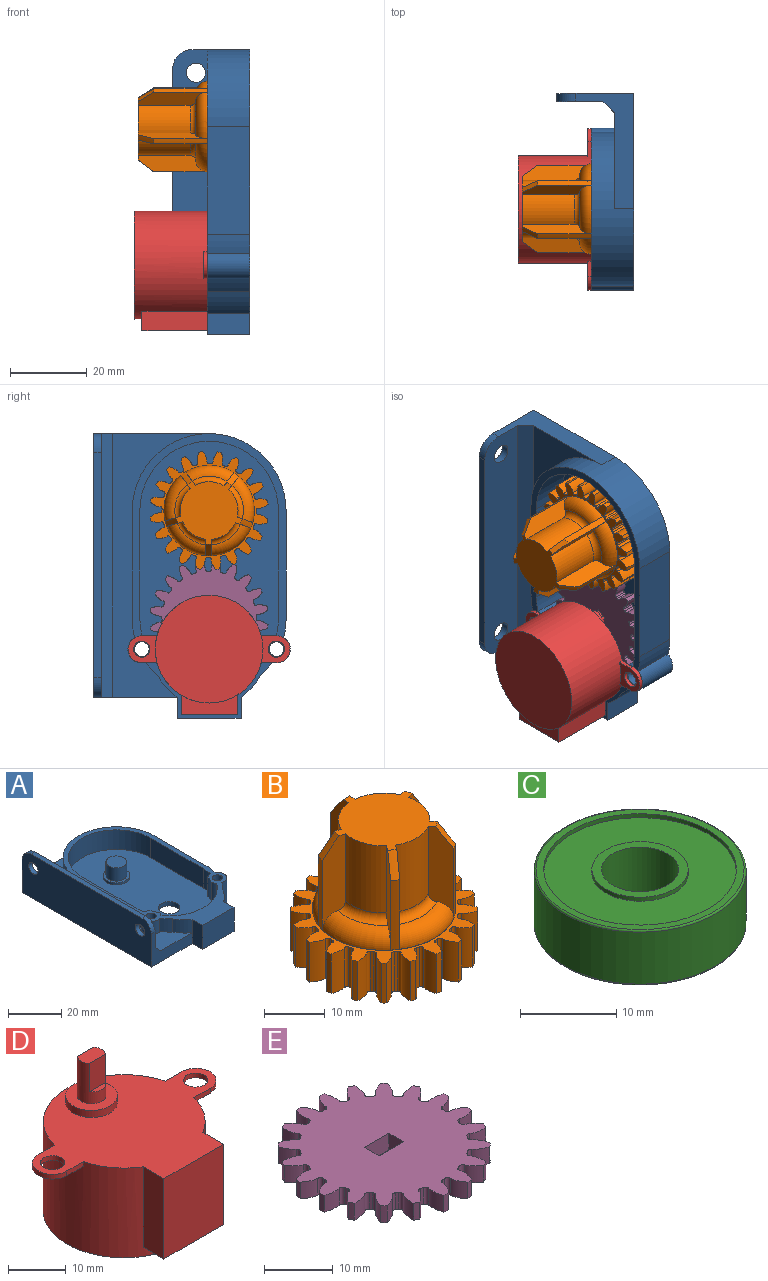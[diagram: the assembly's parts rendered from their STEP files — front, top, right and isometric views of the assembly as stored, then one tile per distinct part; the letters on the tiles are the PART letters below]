
ASSEMBLY  parts=5 mates=4
PART A: 47 faces, bbox 51.1x74x20 mm
  f0: cylinder r=3.6mm len=9mm, axis (0,0,-1), area 19.2mm2, adj f10,f23,f31,f46
  f1: cylinder r=3.6mm len=9mm, axis (0,0,-1), area 19.2mm2, adj f10,f13,f31,f45
  f2: plane 68.49x12mm, normal (1,0,0), area 771.9mm2, adj f36,f37,f39,f40,f41,f42,f43,f44
  f3: plane 68.49x20mm, normal (-1,0,0), area 1319.9mm2, adj f11,f36,f37,f39,f41,f42,f43,f44
  f4: cylinder r=20mm len=11mm, axis (0,0,-1), area 54.8mm2, adj f5,f11,f15,f31
  f5: plane 28x11mm, normal (1,0,0), area 308mm2, adj f4,f6,f11,f31
  f6: cylinder r=20mm len=40mm, axis (0,0,-1), area 534.1mm2, adj f5,f7,f11,f31,f36,f38
  f7: plane 28x6mm, normal (-1,0,0), area 168mm2, adj f6,f8,f31,f38
  f8: cylinder r=20mm len=6mm, axis (0,0,-1), area 29.9mm2, adj f7,f16,f31,f38
  f9: cylinder r=4mm len=8mm, axis (0,0,-1), area 50.3mm2, adj f10,f11
  f10: plane 64x36mm, normal (0,0,1), area 1878.3mm2, adj f0,f1,f9,f12,f13,f14,f23,f24
  f11: plane 74x51.1mm, normal (0,0,-1), area 3293.5mm2, adj f3,f4,f5,f6,f9,f15,f19,f20
  f12: cylinder r=3.6mm len=9mm, axis (0,0,-1), area 19.2mm2, adj f10,f13,f31,f46
  f13: cylinder r=18mm len=29.5mm, axis (0,0,-1), area 311.1mm2, adj f1,f10,f12,f31
  f14: cylinder r=3.6mm len=9mm, axis (0,0,-1), area 19.2mm2, adj f10,f24,f31,f45
  f15: cylinder r=3.6mm len=11mm, axis (0,0,-1), area 114.8mm2, adj f4,f11,f28,f31
  f16: cylinder r=3.6mm len=6.67mm, axis (0,0,-1), area 62.6mm2, adj f8,f17,f31,f38
  f17: cylinder r=20mm len=6mm, axis (0,0,-1), area 28.2mm2, adj f16,f18,f31,f38
  f18: cylinder r=15mm len=6mm, axis (0,0,-1), area 45.3mm2, adj f17,f19,f31,f38
  f19: plane 11x5.51mm, normal (-1,0,0), area 60.6mm2, adj f11,f18,f20,f31,f37
  f20: plane 16.6x11mm, normal (0,-1,0), area 182.6mm2, adj f11,f19,f21,f31
  f21: plane 11x5.51mm, normal (1,0,0), area 60.6mm2, adj f11,f20,f22,f31
  f22: cylinder r=15mm len=11mm, axis (0,0,-1), area 83.1mm2, adj f11,f21,f28,f31
  f23: cylinder r=18mm len=9mm, axis (0,0,-1), area 40mm2, adj f0,f10,f29,f31
  f24: cylinder r=18mm len=9mm, axis (0,0,-1), area 40mm2, adj f10,f14,f25,f31
  f25: plane 28x9mm, normal (1,0,0), area 252mm2, adj f10,f24,f26,f31
  f26: cylinder r=18mm len=36mm, axis (0,0,-1), area 508.9mm2, adj f10,f25,f29,f31
  f27: cylinder r=1.9mm len=11mm, axis (0,0,-1), area 131.3mm2, adj f11,f31
  f28: cylinder r=20mm len=11mm, axis (0,0,-1), area 51.7mm2, adj f11,f15,f22,f31
  f29: plane 28x9mm, normal (-1,0,0), area 252mm2, adj f10,f23,f26,f31
  f30: cylinder r=1.9mm len=11mm, axis (0,0,-1), area 131.3mm2, adj f11,f31
  f31: plane 74x42.2mm, normal (0,0,1), area 502.1mm2, adj f0,f1,f4,f5,f6,f7,f8,f12
  f32: cylinder r=5mm len=10mm, axis (0,0,-1), area 31.4mm2, adj f10,f33
  f33: plane 10x10mm, normal (0,0,1), area 30.8mm2, adj f32,f35
  f34: plane 7.8x7.8mm, normal (0,0,1), area 47.8mm2, adj f35
  f35: cylinder r=3.9mm len=7.8mm, axis (0,0,-1), area 147mm2, adj f33,f34
  f36: plane 30x15mm, normal (0,1,0), area 174.5mm2, adj f2,f3,f6,f11,f38,f40,f43
  f37: plane 21.7x15mm, normal (0,-1,0), area 133mm2, adj f2,f3,f11,f19,f38,f40,f44
  f38: plane 68.49x25mm, normal (0,0,1), area 492.1mm2, adj f6,f7,f8,f16,f17,f18,f36,f37
  f39: plane 58.49x2mm, normal (0,0,1), area 117mm2, adj f2,f3,f43,f44
  f40: plane 68.49x3mm, normal (0.71,0,0.71), area 290.6mm2, adj f2,f36,f37,f38
  f41: cylinder r=2.5mm len=5mm, axis (1,0,0), area 31.4mm2, adj f2,f3
  f42: cylinder r=2.5mm len=5mm, axis (1,0,0), area 31.4mm2, adj f2,f3
  f43: cylinder r=5mm len=5mm, axis (1,0,0), area 15.7mm2, adj f2,f3,f36,f39
  f44: cylinder r=5mm len=5mm, axis (-1,0,0), area 15.7mm2, adj f2,f3,f37,f39
  f45: cylinder r=16.25mm len=9mm, axis (0,0,1), area 33.1mm2, adj f1,f10,f14,f31
  f46: cylinder r=16.25mm len=9mm, axis (0,0,1), area 33.1mm2, adj f0,f10,f12,f31
PART B: 156 faces, bbox 30.6x30.6x26 mm
  f0: cylinder r=15.4mm len=8mm, axis (0,0,-1), area 7.8mm2, adj f19,f21,f72,f119
  f1: cylinder r=15.4mm len=8mm, axis (0,0,-1), area 7.8mm2, adj f19,f21,f114,f117
  f2: cylinder r=15.4mm len=8mm, axis (0,0,-1), area 7.8mm2, adj f19,f21,f109,f112
  f3: cylinder r=15.4mm len=8mm, axis (0,0,-1), area 7.8mm2, adj f19,f21,f104,f107
  f4: cylinder r=15.4mm len=8mm, axis (0,0,-1), area 7.8mm2, adj f19,f21,f99,f102
  f5: cylinder r=15.4mm len=8mm, axis (0,0,-1), area 7.8mm2, adj f19,f21,f94,f97
  f6: cylinder r=15.4mm len=8mm, axis (0,0,-1), area 7.8mm2, adj f19,f21,f89,f92
  f7: cylinder r=15.4mm len=8mm, axis (0,0,-1), area 7.8mm2, adj f19,f21,f84,f87
  f8: cylinder r=15.4mm len=8mm, axis (0,0,-1), area 7.8mm2, adj f19,f21,f67,f79
  f9: cylinder r=15.4mm len=8mm, axis (0,0,-1), area 7.8mm2, adj f19,f21,f74,f77
  f10: cylinder r=15.4mm len=8mm, axis (0,0,-1), area 7.8mm2, adj f19,f21,f62,f69
  f11: cylinder r=15.4mm len=8mm, axis (0,0,-1), area 7.8mm2, adj f19,f21,f42,f64
  f12: cylinder r=15.4mm len=8mm, axis (0,0,-1), area 7.8mm2, adj f19,f21,f22,f59
  f13: cylinder r=15.4mm len=8mm, axis (0,0,-1), area 7.8mm2, adj f19,f21,f54,f57
  f14: cylinder r=15.4mm len=8mm, axis (0,0,-1), area 7.8mm2, adj f19,f21,f49,f52
  f15: cylinder r=15.4mm len=8mm, axis (0,0,-1), area 7.8mm2, adj f19,f21,f44,f47
  f16: cylinder r=15.4mm len=8mm, axis (0,0,-1), area 7.8mm2, adj f19,f21,f32,f39
  f17: cylinder r=15.4mm len=8mm, axis (0,0,-1), area 7.8mm2, adj f19,f21,f34,f82
  f18: cylinder r=15.4mm len=8mm, axis (0,0,-1), area 7.8mm2, adj f19,f21,f29,f37
  f19: plane 30.58x30.58mm, normal (0,0,1), area 169.5mm2, adj f0,f1,f2,f3,f4,f5,f6,f7
  f20: cylinder r=15.4mm len=8mm, axis (0,0,-1), area 7.8mm2, adj f19,f21,f24,f27
  f21: plane 30.58x30.58mm, normal (0,0,-1), area 216.2mm2, adj f0,f1,f2,f3,f4,f5,f6,f7
  f22: extruded ~8x2.51mm, area 22.5mm2, adj f12,f19,f21,f25
  f23: cylinder r=12.25mm len=8mm, axis (0,0,-1), area 4mm2, adj f19,f21,f25,f26
  f24: extruded ~8x2.51mm, area 22.5mm2, adj f19,f20,f21,f26
  f25: cylinder r=0.55mm len=8mm, axis (0,0,-1), area 6.8mm2, adj f19,f21,f22,f23
  f26: cylinder r=0.55mm len=8mm, axis (0,0,-1), area 6.8mm2, adj f19,f21,f23,f24
  f27: extruded ~8x2.73mm, area 22.5mm2, adj f19,f20,f21,f30
  f28: cylinder r=12.25mm len=8mm, axis (0,0,-1), area 4mm2, adj f19,f21,f30,f31
  f29: extruded ~8x2.05mm, area 22.5mm2, adj f18,f19,f21,f31
  f30: cylinder r=0.55mm len=8mm, axis (0,0,-1), area 6.8mm2, adj f19,f21,f27,f28
  f31: cylinder r=0.55mm len=8mm, axis (0,0,-1), area 6.8mm2, adj f19,f21,f28,f29
  f32: extruded ~8x2.38mm, area 22.5mm2, adj f16,f19,f21,f35
  f33: cylinder r=12.25mm len=8mm, axis (0,0,-1), area 4mm2, adj f19,f21,f35,f36
  f34: extruded ~8x2.69mm, area 22.5mm2, adj f17,f19,f21,f36
  f35: cylinder r=0.55mm len=8mm, axis (0,0,-1), area 6.8mm2, adj f19,f21,f32,f33
  f36: cylinder r=0.55mm len=8mm, axis (0,0,-1), area 6.8mm2, adj f19,f21,f33,f34
  f37: extruded ~8x2.69mm, area 22.5mm2, adj f18,f19,f21,f40
  f38: cylinder r=12.25mm len=8mm, axis (0,0,-1), area 4mm2, adj f19,f21,f40,f41
  f39: extruded ~8x2.38mm, area 22.5mm2, adj f16,f19,f21,f41
  f40: cylinder r=0.55mm len=8mm, axis (0,0,-1), area 6.8mm2, adj f19,f21,f37,f38
  f41: cylinder r=0.55mm len=8mm, axis (0,0,-1), area 6.8mm2, adj f19,f21,f38,f39
  f42: extruded ~8x2.73mm, area 22.5mm2, adj f11,f19,f21,f45
  f43: cylinder r=12.25mm len=8mm, axis (0,0,-1), area 4mm2, adj f19,f21,f45,f46
  f44: extruded ~8x2.05mm, area 22.5mm2, adj f15,f19,f21,f46
  f45: cylinder r=0.55mm len=8mm, axis (0,0,-1), area 6.8mm2, adj f19,f21,f42,f43
  f46: cylinder r=0.55mm len=8mm, axis (0,0,-1), area 6.8mm2, adj f19,f21,f43,f44
  f47: extruded ~8x2.69mm, area 22.5mm2, adj f15,f19,f21,f50
  f48: cylinder r=12.25mm len=8mm, axis (0,0,-1), area 4mm2, adj f19,f21,f50,f51
  f49: extruded ~8x2.38mm, area 22.5mm2, adj f14,f19,f21,f51
  f50: cylinder r=0.55mm len=8mm, axis (0,0,-1), area 6.8mm2, adj f19,f21,f47,f48
  f51: cylinder r=0.55mm len=8mm, axis (0,0,-1), area 6.8mm2, adj f19,f21,f48,f49
  f52: extruded ~8x2.38mm, area 22.5mm2, adj f14,f19,f21,f55
  f53: cylinder r=12.25mm len=8mm, axis (0,0,-1), area 4mm2, adj f19,f21,f55,f56
  f54: extruded ~8x2.69mm, area 22.5mm2, adj f13,f19,f21,f56
  f55: cylinder r=0.55mm len=8mm, axis (0,0,-1), area 6.8mm2, adj f19,f21,f52,f53
  f56: cylinder r=0.55mm len=8mm, axis (0,0,-1), area 6.8mm2, adj f19,f21,f53,f54
  f57: extruded ~8x2.05mm, area 22.5mm2, adj f13,f19,f21,f60
  f58: cylinder r=12.25mm len=8mm, axis (0,0,-1), area 4mm2, adj f19,f21,f60,f61
  f59: extruded ~8x2.73mm, area 22.5mm2, adj f12,f19,f21,f61
  f60: cylinder r=0.55mm len=8mm, axis (0,0,-1), area 6.8mm2, adj f19,f21,f57,f58
  f61: cylinder r=0.55mm len=8mm, axis (0,0,-1), area 6.8mm2, adj f19,f21,f58,f59
  f62: extruded ~8x2.51mm, area 22.5mm2, adj f10,f19,f21,f65
  f63: cylinder r=12.25mm len=8mm, axis (0,0,-1), area 4mm2, adj f19,f21,f65,f66
  f64: extruded ~8x2.51mm, area 22.5mm2, adj f11,f19,f21,f66
  f65: cylinder r=0.55mm len=8mm, axis (0,0,-1), area 6.8mm2, adj f19,f21,f62,f63
  f66: cylinder r=0.55mm len=8mm, axis (0,0,-1), area 6.8mm2, adj f19,f21,f63,f64
  f67: extruded ~8x2.05mm, area 22.5mm2, adj f8,f19,f21,f70
  f68: cylinder r=12.25mm len=8mm, axis (0,0,-1), area 4mm2, adj f19,f21,f70,f71
  f69: extruded ~8x2.73mm, area 22.5mm2, adj f10,f19,f21,f71
  f70: cylinder r=0.55mm len=8mm, axis (0,0,-1), area 6.8mm2, adj f19,f21,f67,f68
  f71: cylinder r=0.55mm len=8mm, axis (0,0,-1), area 6.8mm2, adj f19,f21,f68,f69
  f72: extruded ~8x2.69mm, area 22.5mm2, adj f0,f19,f21,f75
  f73: cylinder r=12.25mm len=8mm, axis (0,0,-1), area 4mm2, adj f19,f21,f75,f76
  f74: extruded ~8x2.38mm, area 22.5mm2, adj f9,f19,f21,f76
  f75: cylinder r=0.55mm len=8mm, axis (0,0,-1), area 6.8mm2, adj f19,f21,f72,f73
  f76: cylinder r=0.55mm len=8mm, axis (0,0,-1), area 6.8mm2, adj f19,f21,f73,f74
  f77: extruded ~8x2.38mm, area 22.5mm2, adj f9,f19,f21,f80
  f78: cylinder r=12.25mm len=8mm, axis (0,0,-1), area 4mm2, adj f19,f21,f80,f81
  f79: extruded ~8x2.69mm, area 22.5mm2, adj f8,f19,f21,f81
  f80: cylinder r=0.55mm len=8mm, axis (0,0,-1), area 6.8mm2, adj f19,f21,f77,f78
  f81: cylinder r=0.55mm len=8mm, axis (0,0,-1), area 6.8mm2, adj f19,f21,f78,f79
  f82: extruded ~8x2.05mm, area 22.5mm2, adj f17,f19,f21,f85
  f83: cylinder r=12.25mm len=8mm, axis (0,0,-1), area 4mm2, adj f19,f21,f85,f86
  f84: extruded ~8x2.73mm, area 22.5mm2, adj f7,f19,f21,f86
  f85: cylinder r=0.55mm len=8mm, axis (0,0,-1), area 6.8mm2, adj f19,f21,f82,f83
  f86: cylinder r=0.55mm len=8mm, axis (0,0,-1), area 6.8mm2, adj f19,f21,f83,f84
  f87: extruded ~8x2.51mm, area 22.5mm2, adj f7,f19,f21,f90
  f88: cylinder r=12.25mm len=8mm, axis (0,0,-1), area 4mm2, adj f19,f21,f90,f91
  f89: extruded ~8x2.51mm, area 22.5mm2, adj f6,f19,f21,f91
  f90: cylinder r=0.55mm len=8mm, axis (0,0,-1), area 6.8mm2, adj f19,f21,f87,f88
  f91: cylinder r=0.55mm len=8mm, axis (0,0,-1), area 6.8mm2, adj f19,f21,f88,f89
  f92: extruded ~8x2.73mm, area 22.5mm2, adj f6,f19,f21,f95
  f93: cylinder r=12.25mm len=8mm, axis (0,0,-1), area 4mm2, adj f19,f21,f95,f96
  f94: extruded ~8x2.05mm, area 22.5mm2, adj f5,f19,f21,f96
  f95: cylinder r=0.55mm len=8mm, axis (0,0,-1), area 6.8mm2, adj f19,f21,f92,f93
  f96: cylinder r=0.55mm len=8mm, axis (0,0,-1), area 6.8mm2, adj f19,f21,f93,f94
  f97: extruded ~8x2.69mm, area 22.5mm2, adj f5,f19,f21,f100
  f98: cylinder r=12.25mm len=8mm, axis (0,0,-1), area 4mm2, adj f19,f21,f100,f101
  f99: extruded ~8x2.38mm, area 22.5mm2, adj f4,f19,f21,f101
  f100: cylinder r=0.55mm len=8mm, axis (0,0,-1), area 6.8mm2, adj f19,f21,f97,f98
  f101: cylinder r=0.55mm len=8mm, axis (0,0,-1), area 6.8mm2, adj f19,f21,f98,f99
  f102: extruded ~8x2.38mm, area 22.5mm2, adj f4,f19,f21,f105
  f103: cylinder r=12.25mm len=8mm, axis (0,0,-1), area 4mm2, adj f19,f21,f105,f106
  f104: extruded ~8x2.69mm, area 22.5mm2, adj f3,f19,f21,f106
  f105: cylinder r=0.55mm len=8mm, axis (0,0,-1), area 6.8mm2, adj f19,f21,f102,f103
  f106: cylinder r=0.55mm len=8mm, axis (0,0,-1), area 6.8mm2, adj f19,f21,f103,f104
  f107: extruded ~8x2.05mm, area 22.5mm2, adj f3,f19,f21,f110
  f108: cylinder r=12.25mm len=8mm, axis (0,0,-1), area 4mm2, adj f19,f21,f110,f111
  f109: extruded ~8x2.73mm, area 22.5mm2, adj f2,f19,f21,f111
  f110: cylinder r=0.55mm len=8mm, axis (0,0,-1), area 6.8mm2, adj f19,f21,f107,f108
  f111: cylinder r=0.55mm len=8mm, axis (0,0,-1), area 6.8mm2, adj f19,f21,f108,f109
  f112: extruded ~8x2.51mm, area 22.5mm2, adj f2,f19,f21,f115
  f113: cylinder r=12.25mm len=8mm, axis (0,0,-1), area 4mm2, adj f19,f21,f115,f116
  f114: extruded ~8x2.51mm, area 22.5mm2, adj f1,f19,f21,f116
  f115: cylinder r=0.55mm len=8mm, axis (0,0,-1), area 6.8mm2, adj f19,f21,f112,f113
  f116: cylinder r=0.55mm len=8mm, axis (0,0,-1), area 6.8mm2, adj f19,f21,f113,f114
  f117: extruded ~8x2.73mm, area 22.5mm2, adj f1,f19,f21,f120
  f118: cylinder r=12.25mm len=8mm, axis (0,0,-1), area 4mm2, adj f19,f21,f120,f121
  f119: extruded ~8x2.05mm, area 22.5mm2, adj f0,f19,f21,f121
  f120: cylinder r=0.55mm len=8mm, axis (0,0,-1), area 6.8mm2, adj f19,f21,f117,f118
  f121: cylinder r=0.55mm len=8mm, axis (0,0,-1), area 6.8mm2, adj f19,f21,f118,f119
  f122: cylinder r=11.75mm len=23.5mm, axis (0,0,-1), area 105.5mm2, adj f19,f124,f125,f127,f128,f130,f131,f133
  f123: cylinder r=7.5mm len=13.5mm, axis (0,0,-1), area 107mm2, adj f124,f137,f138,f150
  f124: plane 18.04x3.49mm, normal (-0.81,-0.59,0), area 59.4mm2, adj f122,f123,f138,f140,f150,f151
  f125: plane 18.04x3.49mm, normal (0.81,0.59,0), area 59.4mm2, adj f122,f126,f138,f140,f149,f155
  f126: cylinder r=7.5mm len=13.5mm, axis (0,0,-1), area 107mm2, adj f125,f127,f138,f149
  f127: plane 18.04x4.1mm, normal (0.31,-0.95,0), area 59.4mm2, adj f122,f126,f138,f139,f149,f155
  f128: plane 18.04x4.1mm, normal (-0.31,0.95,0), area 59.4mm2, adj f122,f129,f138,f139,f148,f154
  f129: cylinder r=7.5mm len=13.5mm, axis (0,0,-1), area 107mm2, adj f128,f130,f138,f148
  f130: plane 18.04x4.31mm, normal (1,0,0), area 59.4mm2, adj f122,f129,f138,f142,f148,f154
  f131: plane 18.04x4.31mm, normal (-1,0,0), area 59.4mm2, adj f122,f132,f138,f142,f147,f153
  f132: cylinder r=7.5mm len=13.5mm, axis (0,0,-1), area 107mm2, adj f131,f133,f138,f147
  f133: plane 18.04x4.1mm, normal (0.31,0.95,0), area 59.4mm2, adj f122,f132,f138,f143,f147,f153
  f134: plane 18.04x4.1mm, normal (-0.31,-0.95,0), area 59.4mm2, adj f122,f135,f138,f143,f146,f152
  f135: cylinder r=7.5mm len=13.5mm, axis (0,0,-1), area 107mm2, adj f134,f136,f138,f146
  f136: plane 18.04x3.49mm, normal (-0.81,0.59,0), area 59.4mm2, adj f122,f135,f138,f141,f146,f152
  f137: plane 18.04x3.49mm, normal (0.81,-0.59,0), area 59.4mm2, adj f122,f123,f138,f141,f150,f151
  f138: plane 17.05x16.25mm, normal (0,0,1), area 186.1mm2, adj f123,f124,f125,f126,f127,f128,f129,f130
  f139: cone r=8.75mm half-angle=36.9deg, axis (0,0,-1), area 7.6mm2, adj f122,f127,f128,f138
  f140: cone r=8.75mm half-angle=36.9deg, axis (0,0,-1), area 7.6mm2, adj f122,f124,f125,f138
  f141: cone r=8.75mm half-angle=36.9deg, axis (0,0,-1), area 7.6mm2, adj f122,f136,f137,f138
  f142: cone r=8.75mm half-angle=36.9deg, axis (0,0,-1), area 7.6mm2, adj f122,f130,f131,f138
  f143: cone r=8.75mm half-angle=36.9deg, axis (0,0,-1), area 7.6mm2, adj f122,f133,f134,f138
  f144: cylinder r=11.1mm len=22.2mm, axis (0,0,-1), area 557.9mm2, adj f21,f145
  f145: plane 22.2x22.2mm, normal (0,0,-1), area 387.1mm2, adj f144
  f146: torus R=9mm, axis (0,0,1), area 19.5mm2, adj f134,f135,f136,f152
  f147: torus R=9mm, axis (0,0,1), area 19.5mm2, adj f131,f132,f133,f153
  f148: torus R=9mm, axis (0,0,1), area 19.5mm2, adj f128,f129,f130,f154
  f149: torus R=9mm, axis (0,0,1), area 19.5mm2, adj f125,f126,f127,f155
  f150: torus R=9mm, axis (0,0,1), area 19.5mm2, adj f123,f124,f137,f151
  f151: torus R=8.75mm, axis (0,0,-1), area 54.5mm2, adj f122,f124,f137,f150
  f152: torus R=8.75mm, axis (0,0,-1), area 54.5mm2, adj f122,f134,f136,f146
  f153: torus R=8.75mm, axis (0,0,-1), area 54.4mm2, adj f122,f131,f133,f147
  f154: torus R=8.75mm, axis (0,0,-1), area 54.4mm2, adj f122,f128,f130,f148
  f155: torus R=8.75mm, axis (0,0,-1), area 54.4mm2, adj f122,f125,f127,f149
PART C: 14 faces, bbox 23.8x23.8x7 mm
  f0: plane 10x10mm, normal (0,0,-1), area 28.3mm2, adj f2,f9
  f1: plane 10x10mm, normal (0,0,1), area 28.3mm2, adj f2,f6
  f2: cylinder r=4mm len=8mm, axis (0,0,-1), area 175.9mm2, adj f0,f1
  f3: cylinder r=11mm len=22mm, axis (0,0,-1), area 456.2mm2, adj f12,f13
  f4: plane 21.6x21.6mm, normal (0,0,1), area 52.3mm2, adj f7,f13
  f5: plane 21.6x21.6mm, normal (0,0,-1), area 52.3mm2, adj f10,f12
  f6: cylinder r=5mm len=10mm, axis (0,0,1), area 15.7mm2, adj f1,f8
  f7: cylinder r=10mm len=20mm, axis (0,0,1), area 31.4mm2, adj f4,f8
  f8: plane 20x20mm, normal (0,0,1), area 235.6mm2, adj f6,f7
  f9: cylinder r=5mm len=10mm, axis (0,0,-1), area 15.7mm2, adj f0,f11
  f10: cylinder r=10mm len=20mm, axis (0,0,-1), area 31.4mm2, adj f5,f11
  f11: plane 20x20mm, normal (0,0,-1), area 235.6mm2, adj f9,f10
  f12: torus R=10.8mm, axis (0,0,1), area 21.6mm2, adj f3,f5
  f13: torus R=10.8mm, axis (0,0,1), area 21.6mm2, adj f3,f4
PART D: 25 faces, bbox 42x31x29 mm
  f0: plane 28x28mm, normal (0,0,-1), area 615.8mm2, adj f11
  f1: plane 17x5.05mm, normal (-1,0,0), area 85.9mm2, adj f2,f11,f13,f16
  f2: plane 17x14.6mm, normal (0,-1,0), area 248.2mm2, adj f1,f3,f13,f16
  f3: plane 17x5.05mm, normal (1,0,0), area 85.9mm2, adj f2,f11,f13,f16
  f4: plane 3.94x1mm, normal (0,-1,0), area 3.9mm2, adj f5,f11,f13,f14
  f5: cylinder r=3.5mm len=7mm, axis (0,0,-1), area 11mm2, adj f4,f6,f13,f14
  f6: plane 3.94x1mm, normal (0,1,0), area 3.9mm2, adj f5,f11,f13,f14
  f7: plane 3.94x1mm, normal (0,1,0), area 3.9mm2, adj f8,f11,f13,f15
  f8: cylinder r=3.5mm len=7mm, axis (0,0,-1), area 11mm2, adj f7,f9,f13,f15
  f9: plane 3.94x1mm, normal (0,-1,0), area 3.9mm2, adj f8,f11,f13,f15
  f10: cylinder r=2.1mm len=4.2mm, axis (0,0,-1), area 13.2mm2, adj f13,f15
  f11: cylinder r=14mm len=28mm, axis (0,0,-1), area 1396.1mm2, adj f0,f1,f3,f4,f6,f7,f9,f13
  f12: cylinder r=2.1mm len=4.2mm, axis (0,0,-1), area 13.2mm2, adj f13,f14
  f13: plane 42x31mm, normal (0,0,1), area 667.5mm2, adj f1,f2,f3,f4,f5,f6,f7,f8
  f14: plane 7.44x7mm, normal (0,0,-1), area 30.9mm2, adj f4,f5,f6,f11,f12
  f15: plane 7.44x7mm, normal (0,0,-1), area 30.9mm2, adj f7,f8,f9,f10,f11
  f16: plane 14.6x5.05mm, normal (0,0,-1), area 53.5mm2, adj f1,f2,f3,f11
  f17: cylinder r=4.5mm len=9mm, axis (0,0,-1), area 42.4mm2, adj f13,f18
  f18: plane 9x9mm, normal (0,0,1), area 44mm2, adj f17,f19
  f19: cylinder r=2.5mm len=8.5mm, axis (0,0,-1), area 77.9mm2, adj f18,f20,f21,f22,f23,f24
  f20: plane 4x1mm, normal (0,0,1), area 2.8mm2, adj f19,f22
  f21: plane 4x1mm, normal (0,0,1), area 2.8mm2, adj f19,f23
  f22: plane 6x4mm, normal (0,1,0), area 24mm2, adj f19,f20,f24
  f23: plane 6x4mm, normal (0,-1,0), area 24mm2, adj f19,f21,f24
  f24: plane 5x3mm, normal (0,0,1), area 14mm2, adj f19,f22,f23
PART E: 126 faces, bbox 30.6x30.6x3 mm
  f0: cylinder r=15.4mm len=3mm, axis (0,0,-1), area 2.9mm2, adj f19,f21,f72,f119
  f1: cylinder r=15.4mm len=3mm, axis (0,0,-1), area 2.9mm2, adj f19,f21,f114,f117
  f2: cylinder r=15.4mm len=3mm, axis (0,0,-1), area 2.9mm2, adj f19,f21,f109,f112
  f3: cylinder r=15.4mm len=3mm, axis (0,0,-1), area 2.9mm2, adj f19,f21,f104,f107
  f4: cylinder r=15.4mm len=3mm, axis (0,0,-1), area 2.9mm2, adj f19,f21,f99,f102
  f5: cylinder r=15.4mm len=3mm, axis (0,0,-1), area 2.9mm2, adj f19,f21,f94,f97
  f6: cylinder r=15.4mm len=3mm, axis (0,0,-1), area 2.9mm2, adj f19,f21,f89,f92
  f7: cylinder r=15.4mm len=3mm, axis (0,0,-1), area 2.9mm2, adj f19,f21,f84,f87
  f8: cylinder r=15.4mm len=3mm, axis (0,0,-1), area 2.9mm2, adj f19,f21,f67,f79
  f9: cylinder r=15.4mm len=3mm, axis (0,0,-1), area 2.9mm2, adj f19,f21,f74,f77
  f10: cylinder r=15.4mm len=3mm, axis (0,0,-1), area 2.9mm2, adj f19,f21,f62,f69
  f11: cylinder r=15.4mm len=3mm, axis (0,0,-1), area 2.9mm2, adj f19,f21,f42,f64
  f12: cylinder r=15.4mm len=3mm, axis (0,0,-1), area 2.9mm2, adj f19,f21,f22,f59
  f13: cylinder r=15.4mm len=3mm, axis (0,0,-1), area 2.9mm2, adj f19,f21,f54,f57
  f14: cylinder r=15.4mm len=3mm, axis (0,0,-1), area 2.9mm2, adj f19,f21,f49,f52
  f15: cylinder r=15.4mm len=3mm, axis (0,0,-1), area 2.9mm2, adj f19,f21,f44,f47
  f16: cylinder r=15.4mm len=3mm, axis (0,0,-1), area 2.9mm2, adj f19,f21,f32,f39
  f17: cylinder r=15.4mm len=3mm, axis (0,0,-1), area 2.9mm2, adj f19,f21,f34,f82
  f18: cylinder r=15.4mm len=3mm, axis (0,0,-1), area 2.9mm2, adj f19,f21,f29,f37
  f19: plane 30.58x30.58mm, normal (0,0,1), area 588.3mm2, adj f0,f1,f2,f3,f4,f5,f6,f7
  f20: cylinder r=15.4mm len=3mm, axis (0,0,-1), area 2.9mm2, adj f19,f21,f24,f27
  f21: plane 30.58x30.58mm, normal (0,0,-1), area 588.3mm2, adj f0,f1,f2,f3,f4,f5,f6,f7
  f22: extruded ~3x2.51mm, area 8.4mm2, adj f12,f19,f21,f25
  f23: cylinder r=12.25mm len=3mm, axis (0,0,-1), area 1.5mm2, adj f19,f21,f25,f26
  f24: extruded ~3x2.51mm, area 8.4mm2, adj f19,f20,f21,f26
  f25: cylinder r=0.55mm len=3mm, axis (0,0,-1), area 2.5mm2, adj f19,f21,f22,f23
  f26: cylinder r=0.55mm len=3mm, axis (0,0,-1), area 2.5mm2, adj f19,f21,f23,f24
  f27: extruded ~3x2.73mm, area 8.4mm2, adj f19,f20,f21,f30
  f28: cylinder r=12.25mm len=3mm, axis (0,0,-1), area 1.5mm2, adj f19,f21,f30,f31
  f29: extruded ~3x2.05mm, area 8.4mm2, adj f18,f19,f21,f31
  f30: cylinder r=0.55mm len=3mm, axis (0,0,-1), area 2.5mm2, adj f19,f21,f27,f28
  f31: cylinder r=0.55mm len=3mm, axis (0,0,-1), area 2.5mm2, adj f19,f21,f28,f29
  f32: extruded ~3x2.38mm, area 8.4mm2, adj f16,f19,f21,f35
  f33: cylinder r=12.25mm len=3mm, axis (0,0,-1), area 1.5mm2, adj f19,f21,f35,f36
  f34: extruded ~3x2.69mm, area 8.4mm2, adj f17,f19,f21,f36
  f35: cylinder r=0.55mm len=3mm, axis (0,0,-1), area 2.5mm2, adj f19,f21,f32,f33
  f36: cylinder r=0.55mm len=3mm, axis (0,0,-1), area 2.5mm2, adj f19,f21,f33,f34
  f37: extruded ~3x2.69mm, area 8.4mm2, adj f18,f19,f21,f40
  f38: cylinder r=12.25mm len=3mm, axis (0,0,-1), area 1.5mm2, adj f19,f21,f40,f41
  f39: extruded ~3x2.38mm, area 8.4mm2, adj f16,f19,f21,f41
  f40: cylinder r=0.55mm len=3mm, axis (0,0,-1), area 2.5mm2, adj f19,f21,f37,f38
  f41: cylinder r=0.55mm len=3mm, axis (0,0,-1), area 2.5mm2, adj f19,f21,f38,f39
  f42: extruded ~3x2.73mm, area 8.4mm2, adj f11,f19,f21,f45
  f43: cylinder r=12.25mm len=3mm, axis (0,0,-1), area 1.5mm2, adj f19,f21,f45,f46
  f44: extruded ~3x2.05mm, area 8.4mm2, adj f15,f19,f21,f46
  f45: cylinder r=0.55mm len=3mm, axis (0,0,-1), area 2.5mm2, adj f19,f21,f42,f43
  f46: cylinder r=0.55mm len=3mm, axis (0,0,-1), area 2.5mm2, adj f19,f21,f43,f44
  f47: extruded ~3x2.69mm, area 8.4mm2, adj f15,f19,f21,f50
  f48: cylinder r=12.25mm len=3mm, axis (0,0,-1), area 1.5mm2, adj f19,f21,f50,f51
  f49: extruded ~3x2.38mm, area 8.4mm2, adj f14,f19,f21,f51
  f50: cylinder r=0.55mm len=3mm, axis (0,0,-1), area 2.5mm2, adj f19,f21,f47,f48
  f51: cylinder r=0.55mm len=3mm, axis (0,0,-1), area 2.5mm2, adj f19,f21,f48,f49
  f52: extruded ~3x2.38mm, area 8.4mm2, adj f14,f19,f21,f55
  f53: cylinder r=12.25mm len=3mm, axis (0,0,-1), area 1.5mm2, adj f19,f21,f55,f56
  f54: extruded ~3x2.69mm, area 8.4mm2, adj f13,f19,f21,f56
  f55: cylinder r=0.55mm len=3mm, axis (0,0,-1), area 2.5mm2, adj f19,f21,f52,f53
  f56: cylinder r=0.55mm len=3mm, axis (0,0,-1), area 2.5mm2, adj f19,f21,f53,f54
  f57: extruded ~3x2.05mm, area 8.4mm2, adj f13,f19,f21,f60
  f58: cylinder r=12.25mm len=3mm, axis (0,0,-1), area 1.5mm2, adj f19,f21,f60,f61
  f59: extruded ~3x2.73mm, area 8.4mm2, adj f12,f19,f21,f61
  f60: cylinder r=0.55mm len=3mm, axis (0,0,-1), area 2.5mm2, adj f19,f21,f57,f58
  f61: cylinder r=0.55mm len=3mm, axis (0,0,-1), area 2.5mm2, adj f19,f21,f58,f59
  f62: extruded ~3x2.51mm, area 8.4mm2, adj f10,f19,f21,f65
  f63: cylinder r=12.25mm len=3mm, axis (0,0,-1), area 1.5mm2, adj f19,f21,f65,f66
  f64: extruded ~3x2.51mm, area 8.4mm2, adj f11,f19,f21,f66
  f65: cylinder r=0.55mm len=3mm, axis (0,0,-1), area 2.5mm2, adj f19,f21,f62,f63
  f66: cylinder r=0.55mm len=3mm, axis (0,0,-1), area 2.5mm2, adj f19,f21,f63,f64
  f67: extruded ~3x2.05mm, area 8.4mm2, adj f8,f19,f21,f70
  f68: cylinder r=12.25mm len=3mm, axis (0,0,-1), area 1.5mm2, adj f19,f21,f70,f71
  f69: extruded ~3x2.73mm, area 8.4mm2, adj f10,f19,f21,f71
  f70: cylinder r=0.55mm len=3mm, axis (0,0,-1), area 2.5mm2, adj f19,f21,f67,f68
  f71: cylinder r=0.55mm len=3mm, axis (0,0,-1), area 2.5mm2, adj f19,f21,f68,f69
  f72: extruded ~3x2.69mm, area 8.4mm2, adj f0,f19,f21,f75
  f73: cylinder r=12.25mm len=3mm, axis (0,0,-1), area 1.5mm2, adj f19,f21,f75,f76
  f74: extruded ~3x2.38mm, area 8.4mm2, adj f9,f19,f21,f76
  f75: cylinder r=0.55mm len=3mm, axis (0,0,-1), area 2.5mm2, adj f19,f21,f72,f73
  f76: cylinder r=0.55mm len=3mm, axis (0,0,-1), area 2.5mm2, adj f19,f21,f73,f74
  f77: extruded ~3x2.38mm, area 8.4mm2, adj f9,f19,f21,f80
  f78: cylinder r=12.25mm len=3mm, axis (0,0,-1), area 1.5mm2, adj f19,f21,f80,f81
  f79: extruded ~3x2.69mm, area 8.4mm2, adj f8,f19,f21,f81
  f80: cylinder r=0.55mm len=3mm, axis (0,0,-1), area 2.5mm2, adj f19,f21,f77,f78
  f81: cylinder r=0.55mm len=3mm, axis (0,0,-1), area 2.5mm2, adj f19,f21,f78,f79
  f82: extruded ~3x2.05mm, area 8.4mm2, adj f17,f19,f21,f85
  f83: cylinder r=12.25mm len=3mm, axis (0,0,-1), area 1.5mm2, adj f19,f21,f85,f86
  f84: extruded ~3x2.73mm, area 8.4mm2, adj f7,f19,f21,f86
  f85: cylinder r=0.55mm len=3mm, axis (0,0,-1), area 2.5mm2, adj f19,f21,f82,f83
  f86: cylinder r=0.55mm len=3mm, axis (0,0,-1), area 2.5mm2, adj f19,f21,f83,f84
  f87: extruded ~3x2.51mm, area 8.4mm2, adj f7,f19,f21,f90
  f88: cylinder r=12.25mm len=3mm, axis (0,0,-1), area 1.5mm2, adj f19,f21,f90,f91
  f89: extruded ~3x2.51mm, area 8.4mm2, adj f6,f19,f21,f91
  f90: cylinder r=0.55mm len=3mm, axis (0,0,-1), area 2.5mm2, adj f19,f21,f87,f88
  f91: cylinder r=0.55mm len=3mm, axis (0,0,-1), area 2.5mm2, adj f19,f21,f88,f89
  f92: extruded ~3x2.73mm, area 8.4mm2, adj f6,f19,f21,f95
  f93: cylinder r=12.25mm len=3mm, axis (0,0,-1), area 1.5mm2, adj f19,f21,f95,f96
  f94: extruded ~3x2.05mm, area 8.4mm2, adj f5,f19,f21,f96
  f95: cylinder r=0.55mm len=3mm, axis (0,0,-1), area 2.5mm2, adj f19,f21,f92,f93
  f96: cylinder r=0.55mm len=3mm, axis (0,0,-1), area 2.5mm2, adj f19,f21,f93,f94
  f97: extruded ~3x2.69mm, area 8.4mm2, adj f5,f19,f21,f100
  f98: cylinder r=12.25mm len=3mm, axis (0,0,-1), area 1.5mm2, adj f19,f21,f100,f101
  f99: extruded ~3x2.38mm, area 8.4mm2, adj f4,f19,f21,f101
  f100: cylinder r=0.55mm len=3mm, axis (0,0,-1), area 2.5mm2, adj f19,f21,f97,f98
  f101: cylinder r=0.55mm len=3mm, axis (0,0,-1), area 2.5mm2, adj f19,f21,f98,f99
  f102: extruded ~3x2.38mm, area 8.4mm2, adj f4,f19,f21,f105
  f103: cylinder r=12.25mm len=3mm, axis (0,0,-1), area 1.5mm2, adj f19,f21,f105,f106
  f104: extruded ~3x2.69mm, area 8.4mm2, adj f3,f19,f21,f106
  f105: cylinder r=0.55mm len=3mm, axis (0,0,-1), area 2.5mm2, adj f19,f21,f102,f103
  f106: cylinder r=0.55mm len=3mm, axis (0,0,-1), area 2.5mm2, adj f19,f21,f103,f104
  f107: extruded ~3x2.05mm, area 8.4mm2, adj f3,f19,f21,f110
  f108: cylinder r=12.25mm len=3mm, axis (0,0,-1), area 1.5mm2, adj f19,f21,f110,f111
  f109: extruded ~3x2.73mm, area 8.4mm2, adj f2,f19,f21,f111
  f110: cylinder r=0.55mm len=3mm, axis (0,0,-1), area 2.5mm2, adj f19,f21,f107,f108
  f111: cylinder r=0.55mm len=3mm, axis (0,0,-1), area 2.5mm2, adj f19,f21,f108,f109
  f112: extruded ~3x2.51mm, area 8.4mm2, adj f2,f19,f21,f115
  f113: cylinder r=12.25mm len=3mm, axis (0,0,-1), area 1.5mm2, adj f19,f21,f115,f116
  f114: extruded ~3x2.51mm, area 8.4mm2, adj f1,f19,f21,f116
  f115: cylinder r=0.55mm len=3mm, axis (0,0,-1), area 2.5mm2, adj f19,f21,f112,f113
  f116: cylinder r=0.55mm len=3mm, axis (0,0,-1), area 2.5mm2, adj f19,f21,f113,f114
  f117: extruded ~3x2.73mm, area 8.4mm2, adj f1,f19,f21,f120
  f118: cylinder r=12.25mm len=3mm, axis (0,0,-1), area 1.5mm2, adj f19,f21,f120,f121
  f119: extruded ~3x2.05mm, area 8.4mm2, adj f0,f19,f21,f121
  f120: cylinder r=0.55mm len=3mm, axis (0,0,-1), area 2.5mm2, adj f19,f21,f117,f118
  f121: cylinder r=0.55mm len=3mm, axis (0,0,-1), area 2.5mm2, adj f19,f21,f118,f119
  f122: plane 3x3mm, normal (-1,0,0), area 9mm2, adj f19,f21,f123,f124
  f123: plane 5x3mm, normal (0,1,0), area 15mm2, adj f19,f21,f122,f125
  f124: plane 5x3mm, normal (0,-1,0), area 15mm2, adj f19,f21,f122,f125
  f125: plane 3x3mm, normal (1,0,0), area 9mm2, adj f19,f21,f123,f124
PLACE A rot(axis=(0.58,-0.58,-0.58),120deg) t=(1.43,-26.52,44.35)mm fixed
PLACE B rot(axis=(0.42,-0.81,-0.42),102.3deg) t=(-1.57,-26.52,44.35)mm
PLACE C rot(axis=(0.69,-0.22,-0.69),155.4deg) t=(-1.57,-26.52,44.35)mm
PLACE D rot(axis=(0.58,0.58,0.58),120deg) t=(-28.57,-26.52,8.35)mm
PLACE E rot(axis=(-0.69,-0.22,0.69),155.4deg) t=(-2.07,-26.52,16.35)mm
MATE revolute D.f17 <-> E.f0  axis (1,0,0) through (0.43,-26.52,16.35)mm
MATE fastened D.f10 <-> A.f0  axis (1,0,0) through (-9.57,-44.02,8.35)mm
MATE revolute B.f144 <-> A.f35  axis (1,0,0) through (-1.57,-26.52,44.35)mm
MATE fastened C.f2 <-> B.f154  axis (-1,0,0) through (-8.57,-26.52,44.35)mm
